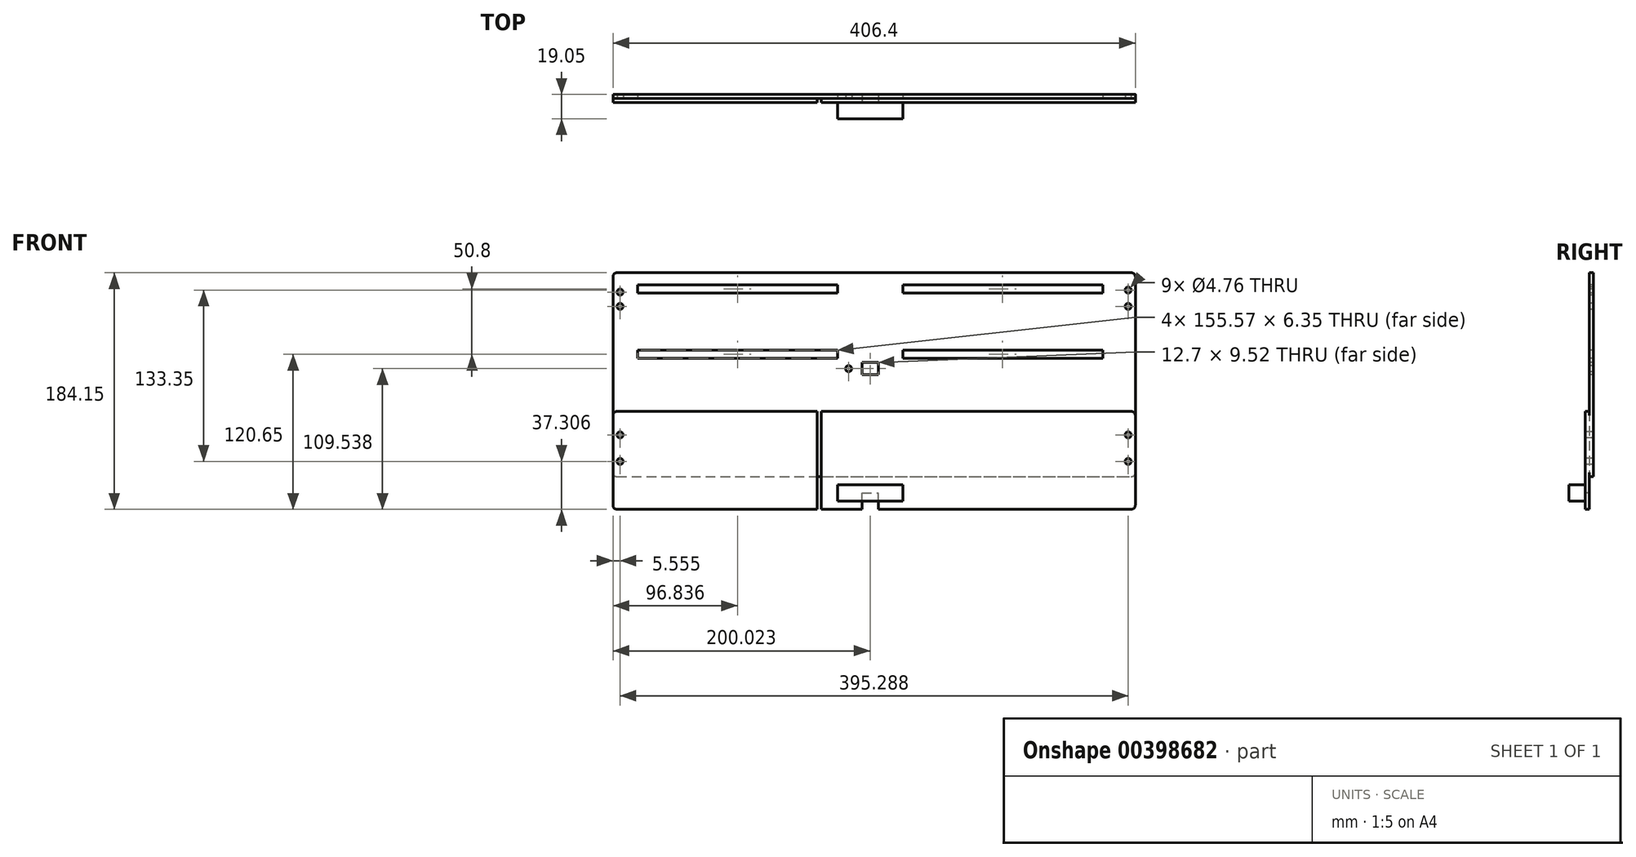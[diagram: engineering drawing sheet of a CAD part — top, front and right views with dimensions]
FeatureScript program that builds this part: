
annotation { "Feature Type Name" : "Feature", "Feature Type Description" : "" }
export const myFeature = defineFeature(function(context is Context, id is Id, definition is map)
    precondition{}
    {
        {
            var Q0;
            Q0=qCreatedBy(makeId("Front.planeOp"),FACE);
            var sketch = newSketch(context, id + "F0", { "sketchPlane" : qUnion([Q0])});
            skLineSegment(sketch, "E0.bottom", {"start": v(-194.67, 58.2) * mm, "end": v(211.73, 58.2) * mm});
            skLineSegment(sketch, "E0.top", {"start": v(-194.67, -100.56) * mm, "end": v(211.73, -100.56) * mm});
            skLineSegment(sketch, "E0.left", {"start": v(-194.67, 58.2) * mm, "end": v(-194.67, -100.56) * mm});
            skLineSegment(sketch, "E0.right", {"start": v(211.73, 58.2) * mm, "end": v(211.73, -100.56) * mm});
            skSolve(sketch);
        }
        {
            var Q0;
            Q0 = qSketchRegion(id + "F0", true);
            extrude(context, id + "F1", {"entities" : qUnion([Q0]), "depth" : 3.17 * mm});
        }
        {
            var Q0;
            Q0=makeQuery(id+"F1.opExtrude","SWEPT_EDGE",EDGE,{"disambiguationData":[OSD([sQuery(id+"F0.wireOp",EDGE,"E0.bottom"),sQuery(id+"F0.wireOp",EDGE,"E0.left")])]});
            fillet(context, id + "F2", {"entities" : qUnion([Q0]), "radius" : 3.17 * mm, "tangentPropagation" : true, "allowEdgeOverflow" : false});
        }
        {
            var Q0;
            Q0=makeQuery(id+"F1.opExtrude","SWEPT_EDGE",EDGE,{"disambiguationData":[OSD([sQuery(id+"F0.wireOp",EDGE,"E0.bottom"),sQuery(id+"F0.wireOp",EDGE,"E0.right")])]});
            fillet(context, id + "F3", {"entities" : qUnion([Q0]), "radius" : 3.17 * mm, "tangentPropagation" : true, "allowEdgeOverflow" : false});
        }
        {
            var Q0;
            Q0=makeQuery(id+"F1.opExtrude","SWEPT_EDGE",EDGE,{"disambiguationData":[OSD([sQuery(id+"F0.wireOp",EDGE,"E0.top"),sQuery(id+"F0.wireOp",EDGE,"E0.right")])]});
            fillet(context, id + "F4", {"entities" : qUnion([Q0]), "radius" : 3.17 * mm, "tangentPropagation" : true, "allowEdgeOverflow" : false});
        }
        {
            var Q0;
            Q0=makeQuery(id+"F1.opExtrude","SWEPT_EDGE",EDGE,{"disambiguationData":[OSD([sQuery(id+"F0.wireOp",EDGE,"E0.top"),sQuery(id+"F0.wireOp",EDGE,"E0.left")])]});
            fillet(context, id + "F5", {"entities" : qUnion([Q0]), "radius" : 3.17 * mm, "tangentPropagation" : true, "allowEdgeOverflow" : false});
        }
        {
            var Q0;
            Q0=makeQuery(id+"F1.opExtrude","CAP_FACE",FACE,{"disambiguationData":[OSD([sQuery(id+"F0.wireOp",EDGE,"E0.bottom"),sQuery(id+"F0.wireOp",EDGE,"E0.top"),sQuery(id+"F0.wireOp",EDGE,"E0.left"),sQuery(id+"F0.wireOp",EDGE,"E0.right")])],"isStart":false});
            var sketch = newSketch(context, id + "F6", { "sketchPlane" : qUnion([Q0])});
            skLineSegment(sketch, "E1.bottom", {"start": v(-175.62, 48.67) * mm, "end": v(-20.05, 48.67) * mm});
            skLineSegment(sketch, "E1.top", {"start": v(-175.62, 42.32) * mm, "end": v(-20.05, 42.32) * mm});
            skLineSegment(sketch, "E1.left", {"start": v(-175.62, 48.67) * mm, "end": v(-175.62, 42.32) * mm});
            skLineSegment(sketch, "E1.right", {"start": v(-20.05, 48.67) * mm, "end": v(-20.05, 42.32) * mm});
            skSolve(sketch);
        }
        {
            var Q0;
            Q0=makeQuery(id+"F6.imprint","IMPRINT",FACE,{"disambiguationData":[TD([[makeQuery(id+"F6.imprint","IMPRINT",EDGE,{"derivedFrom":sQuery(id+"F6.wireOp",EDGE,"E1.bottom")}),-1.0]])]});
            extrude(context, id + "F7", {"entities" : qUnion([Q0]), "operationType" : NewBodyOperationType.REMOVE, "oppositeDirection" : true, "depth" : 3.17 * mm});
        }
        {
            var Q0;
            Q0=makeQuery(id+"F1.opExtrude","CAP_FACE",FACE,{"disambiguationData":[OSD([sQuery(id+"F0.wireOp",EDGE,"E0.bottom"),sQuery(id+"F0.wireOp",EDGE,"E0.top"),sQuery(id+"F0.wireOp",EDGE,"E0.left"),sQuery(id+"F0.wireOp",EDGE,"E0.right")])],"isStart":false});
            var sketch = newSketch(context, id + "F8", { "sketchPlane" : qUnion([Q0])});
            skLineSegment(sketch, "E2.bottom", {"start": v(-175.62, -2.13) * mm, "end": v(-20.05, -2.13) * mm});
            skLineSegment(sketch, "E2.top", {"start": v(-175.62, -8.48) * mm, "end": v(-20.05, -8.48) * mm});
            skLineSegment(sketch, "E2.left", {"start": v(-175.62, -2.13) * mm, "end": v(-175.62, -8.48) * mm});
            skLineSegment(sketch, "E2.right", {"start": v(-20.05, -2.13) * mm, "end": v(-20.05, -8.48) * mm});
            skSolve(sketch);
        }
        {
            var Q0;
            Q0 = qSketchRegion(id + "F8", true);
            extrude(context, id + "F9", {"entities" : qUnion([Q0]), "operationType" : NewBodyOperationType.REMOVE, "oppositeDirection" : true, "depth" : 3.17 * mm});
        }
        {
            var Q0;
            Q0=makeQuery(id+"F1.opExtrude","CAP_FACE",FACE,{"disambiguationData":[OSD([sQuery(id+"F0.wireOp",EDGE,"E0.bottom"),sQuery(id+"F0.wireOp",EDGE,"E0.top"),sQuery(id+"F0.wireOp",EDGE,"E0.left"),sQuery(id+"F0.wireOp",EDGE,"E0.right")])],"isStart":false});
            var sketch = newSketch(context, id + "F10", { "sketchPlane" : qUnion([Q0])});
            skLineSegment(sketch, "E3.bottom", {"start": v(30.75, 48.67) * mm, "end": v(186.33, 48.67) * mm});
            skLineSegment(sketch, "E3.top", {"start": v(30.75, 42.32) * mm, "end": v(186.33, 42.32) * mm});
            skLineSegment(sketch, "E3.left", {"start": v(30.75, 48.67) * mm, "end": v(30.75, 42.32) * mm});
            skLineSegment(sketch, "E3.right", {"start": v(186.33, 48.67) * mm, "end": v(186.33, 42.32) * mm});
            skSolve(sketch);
        }
        {
            var Q0;
            Q0 = qSketchRegion(id + "F10", true);
            extrude(context, id + "F11", {"entities" : qUnion([Q0]), "operationType" : NewBodyOperationType.REMOVE, "oppositeDirection" : true, "depth" : 3.17 * mm});
        }
        {
            var Q0;
            Q0=makeQuery(id+"F1.opExtrude","CAP_FACE",FACE,{"disambiguationData":[OSD([sQuery(id+"F0.wireOp",EDGE,"E0.bottom"),sQuery(id+"F0.wireOp",EDGE,"E0.top"),sQuery(id+"F0.wireOp",EDGE,"E0.left"),sQuery(id+"F0.wireOp",EDGE,"E0.right")])],"isStart":false});
            var sketch = newSketch(context, id + "F12", { "sketchPlane" : qUnion([Q0])});
            skLineSegment(sketch, "E4.bottom", {"start": v(30.75, -2.13) * mm, "end": v(186.33, -2.13) * mm});
            skLineSegment(sketch, "E4.top", {"start": v(30.75, -8.48) * mm, "end": v(186.33, -8.48) * mm});
            skLineSegment(sketch, "E4.left", {"start": v(30.75, -2.13) * mm, "end": v(30.75, -8.48) * mm});
            skLineSegment(sketch, "E4.right", {"start": v(186.33, -2.13) * mm, "end": v(186.33, -8.48) * mm});
            skSolve(sketch);
        }
        {
            var Q0;
            Q0 = qSketchRegion(id + "F12", true);
            extrude(context, id + "F13", {"entities" : qUnion([Q0]), "operationType" : NewBodyOperationType.REMOVE, "oppositeDirection" : true, "depth" : 25.4 * mm});
        }
        {
            var Q0;
            Q0=makeQuery(id+"F1.opExtrude","CAP_FACE",FACE,{"disambiguationData":[OSD([sQuery(id+"F0.wireOp",EDGE,"E0.bottom"),sQuery(id+"F0.wireOp",EDGE,"E0.top"),sQuery(id+"F0.wireOp",EDGE,"E0.left"),sQuery(id+"F0.wireOp",EDGE,"E0.right")])],"isStart":false});
            var sketch = newSketch(context, id + "F14", { "sketchPlane" : qUnion([Q0])});
            skLineSegment(sketch, "E5.bottom", {"start": v(-1, -11.66) * mm, "end": v(11.7, -11.66) * mm});
            skLineSegment(sketch, "E5.top", {"start": v(-1, -21.18) * mm, "end": v(11.7, -21.18) * mm});
            skLineSegment(sketch, "E5.left", {"start": v(-1, -11.66) * mm, "end": v(-1, -21.18) * mm});
            skLineSegment(sketch, "E5.right", {"start": v(11.7, -11.66) * mm, "end": v(11.7, -21.18) * mm});
            skSolve(sketch);
        }
        {
            var Q0;
            Q0 = qSketchRegion(id + "F14", true);
            extrude(context, id + "F15", {"entities" : qUnion([Q0]), "operationType" : NewBodyOperationType.REMOVE, "oppositeDirection" : true, "depth" : 25.4 * mm});
        }
        {
            var Q0;
            Q0=makeQuery(id+"F1.opExtrude","CAP_FACE",FACE,{"disambiguationData":[OSD([sQuery(id+"F0.wireOp",EDGE,"E0.bottom"),sQuery(id+"F0.wireOp",EDGE,"E0.top"),sQuery(id+"F0.wireOp",EDGE,"E0.left"),sQuery(id+"F0.wireOp",EDGE,"E0.right")])],"isStart":false});
            var sketch = newSketch(context, id + "F16", { "sketchPlane" : qUnion([Q0])});
            skCircle(sketch, "E6", {"center": v(-11.32, -16.47) * mm, "radius": 2.38 * mm});
            skSolve(sketch);
        }
        {
            var Q0;
            Q0 = qSketchRegion(id + "F16", true);
            extrude(context, id + "F17", {"entities" : qUnion([Q0]), "operationType" : NewBodyOperationType.REMOVE, "oppositeDirection" : true, "depth" : 3.17 * mm});
        }
        {
            var Q0;
            Q0=makeQuery(id+"F1.opExtrude","CAP_FACE",FACE,{"disambiguationData":[OSD([sQuery(id+"F0.wireOp",EDGE,"E0.bottom"),sQuery(id+"F0.wireOp",EDGE,"E0.top"),sQuery(id+"F0.wireOp",EDGE,"E0.left"),sQuery(id+"F0.wireOp",EDGE,"E0.right")])],"isStart":false});
            var sketch = newSketch(context, id + "F18", { "sketchPlane" : qUnion([Q0])});
            skCircle(sketch, "E7", {"center": v(-189.12, 43.1) * mm, "radius": 2.38 * mm});
            skCircle(sketch, "E8", {"center": v(-189.12, 32) * mm, "radius": 2.38 * mm});
            skSolve(sketch);
        }
        {
            var Q0;
            Q0 = qSketchRegion(id + "F18", true);
            extrude(context, id + "F19", {"entities" : qUnion([Q0]), "operationType" : NewBodyOperationType.REMOVE, "oppositeDirection" : true, "depth" : 25.4 * mm});
        }
        {
            var Q0;
            Q0=makeQuery(id+"F1.opExtrude","CAP_FACE",FACE,{"disambiguationData":[OSD([sQuery(id+"F0.wireOp",EDGE,"E0.bottom"),sQuery(id+"F0.wireOp",EDGE,"E0.top"),sQuery(id+"F0.wireOp",EDGE,"E0.left"),sQuery(id+"F0.wireOp",EDGE,"E0.right")])],"isStart":false});
            var sketch = newSketch(context, id + "F20", { "sketchPlane" : qUnion([Q0])});
            skCircle(sketch, "E9", {"center": v(206.17, 44.7) * mm, "radius": 2.38 * mm});
            skCircle(sketch, "E10", {"center": v(206.17, 32) * mm, "radius": 2.38 * mm});
            skSolve(sketch);
        }
        {
            var Q0;
            Q0=makeQuery(id+"F20.imprint","IMPRINT",FACE,{"disambiguationData":[TD([[makeQuery(id+"F20.imprint","IMPRINT",EDGE,{"derivedFrom":sQuery(id+"F20.wireOp",EDGE,"E9")}),1.0]])]});
            var Q1;
            Q1=makeQuery(id+"F20.imprint","IMPRINT",FACE,{"disambiguationData":[TD([[makeQuery(id+"F20.imprint","IMPRINT",EDGE,{"derivedFrom":sQuery(id+"F20.wireOp",EDGE,"E10")}),1.0]])]});
            extrude(context, id + "F21", {"entities" : qUnion([Q0, Q1]), "operationType" : NewBodyOperationType.REMOVE, "oppositeDirection" : true, "depth" : 25.4 * mm});
        }
        {
            var Q0;
            Q0=makeQuery(id+"F1.opExtrude","CAP_FACE",FACE,{"disambiguationData":[OSD([sQuery(id+"F0.wireOp",EDGE,"E0.bottom"),sQuery(id+"F0.wireOp",EDGE,"E0.top"),sQuery(id+"F0.wireOp",EDGE,"E0.left"),sQuery(id+"F0.wireOp",EDGE,"E0.right")])],"isStart":false});
            var sketch = newSketch(context, id + "F22", { "sketchPlane" : qUnion([Q0])});
            skLineSegment(sketch, "E11.bottom", {"start": v(-194.67, -49.76) * mm, "end": v(211.73, -49.76) * mm});
            skLineSegment(sketch, "E11.top", {"start": v(-194.67, -125.96) * mm, "end": v(211.73, -125.96) * mm});
            skLineSegment(sketch, "E11.left", {"start": v(-194.67, -49.76) * mm, "end": v(-194.67, -125.96) * mm});
            skLineSegment(sketch, "E11.right", {"start": v(211.73, -49.76) * mm, "end": v(211.73, -125.96) * mm});
            skSolve(sketch);
        }
        {
            var Q0;
            Q0 = qSketchRegion(id + "F22", true);
            extrude(context, id + "F23", {"entities" : qUnion([Q0]), "operationType" : NewBodyOperationType.ADD, "depth" : 3.17 * mm});
        }
        {
            var Q0;
            Q0=makeQuery(id+"F23.opExtrude","SWEPT_EDGE",EDGE,{"disambiguationData":[OSD([sQuery(id+"F22.wireOp",EDGE,"E11.top"),sQuery(id+"F22.wireOp",EDGE,"E11.left")])]});
            var Q1;
            Q1=makeQuery(id+"F23.opExtrude","SWEPT_EDGE",EDGE,{"disambiguationData":[OSD([sQuery(id+"F22.wireOp",EDGE,"E11.top"),sQuery(id+"F22.wireOp",EDGE,"E11.right")])]});
            fillet(context, id + "F24", {"entities" : qUnion([Q0, Q1]), "radius" : 3.17 * mm, "tangentPropagation" : true, "allowEdgeOverflow" : false});
        }
        {
            var Q0;
            Q0=makeQuery(id+"F23.opExtrude","SWEPT_EDGE",EDGE,{"disambiguationData":[OSD([sQuery(id+"F0.wireOp",EDGE,"E0.right"),sQuery(id+"F22.wireOp",EDGE,"E11.bottom"),sQuery(id+"F22.wireOp",EDGE,"E11.right")])]});
            var Q1;
            Q1=makeQuery(id+"F23.opExtrude","SWEPT_EDGE",EDGE,{"disambiguationData":[OSD([sQuery(id+"F0.wireOp",EDGE,"E0.left"),sQuery(id+"F22.wireOp",EDGE,"E11.bottom"),sQuery(id+"F22.wireOp",EDGE,"E11.left")])]});
            fillet(context, id + "F25", {"entities" : qUnion([Q0, Q1]), "radius" : 3.17 * mm, "tangentPropagation" : true, "allowEdgeOverflow" : false});
        }
        {
            var Q0;
            Q0=makeQuery(id+"F23.opExtrude","CAP_FACE",FACE,{"disambiguationData":[OSD([sQuery(id+"F22.wireOp",EDGE,"E11.bottom"),sQuery(id+"F22.wireOp",EDGE,"E11.top"),sQuery(id+"F22.wireOp",EDGE,"E11.left"),sQuery(id+"F22.wireOp",EDGE,"E11.right")])],"isStart":false});
            var sketch = newSketch(context, id + "F26", { "sketchPlane" : qUnion([Q0])});
            skLineSegment(sketch, "E12.bottom", {"start": v(-1, -125.96) * mm, "end": v(11.7, -125.96) * mm});
            skLineSegment(sketch, "E12.top", {"start": v(-1, -113.26) * mm, "end": v(11.7, -113.26) * mm});
            skLineSegment(sketch, "E12.left", {"start": v(-1, -125.96) * mm, "end": v(-1, -113.26) * mm});
            skLineSegment(sketch, "E12.right", {"start": v(11.7, -125.96) * mm, "end": v(11.7, -113.26) * mm});
            skSolve(sketch);
        }
        {
            var Q0;
            Q0 = qSketchRegion(id + "F26", true);
            extrude(context, id + "F27", {"entities" : qUnion([Q0]), "operationType" : NewBodyOperationType.REMOVE, "oppositeDirection" : true, "depth" : 25.4 * mm});
        }
        {
            var Q0;
            Q0=makeQuery(id+"F23.opExtrude","CAP_FACE",FACE,{"disambiguationData":[OSD([sQuery(id+"F22.wireOp",EDGE,"E11.bottom"),sQuery(id+"F22.wireOp",EDGE,"E11.top"),sQuery(id+"F22.wireOp",EDGE,"E11.left"),sQuery(id+"F22.wireOp",EDGE,"E11.right")])],"isStart":false});
            var sketch = newSketch(context, id + "F28", { "sketchPlane" : qUnion([Q0])});
            skCircle(sketch, "E13", {"center": v(206.17, -68.02) * mm, "radius": 2.38 * mm});
            skCircle(sketch, "E14", {"center": v(206.17, -88.65) * mm, "radius": 2.38 * mm});
            skCircle(sketch, "E15", {"center": v(-189.12, -68.02) * mm, "radius": 2.38 * mm});
            skCircle(sketch, "E16", {"center": v(-189.12, -88.65) * mm, "radius": 2.38 * mm});
            skSolve(sketch);
        }
        {
            var Q0;
            Q0 = qSketchRegion(id + "F28", true);
            extrude(context, id + "F29", {"entities" : qUnion([Q0]), "operationType" : NewBodyOperationType.REMOVE, "oppositeDirection" : true, "depth" : 25.4 * mm});
        }
        {
            var Q0;
            Q0=makeQuery(id+"F23.opExtrude","CAP_FACE",FACE,{"disambiguationData":[OSD([sQuery(id+"F22.wireOp",EDGE,"E11.bottom"),sQuery(id+"F22.wireOp",EDGE,"E11.top"),sQuery(id+"F22.wireOp",EDGE,"E11.left"),sQuery(id+"F22.wireOp",EDGE,"E11.right")])],"isStart":false});
            var sketch = newSketch(context, id + "F30", { "sketchPlane" : qUnion([Q0])});
            skPoint(sketch, "E17.oppositeSnap0", {"position": v(11.7, -119.6) * mm});
            skLineSegment(sketch, "E17.bottom", {"start": v(-20.05, -106.9) * mm, "end": v(30.75, -106.9) * mm});
            skLineSegment(sketch, "E17.top", {"start": v(-20.05, -119.6) * mm, "end": v(30.75, -119.6) * mm});
            skLineSegment(sketch, "E17.left", {"start": v(-20.05, -106.9) * mm, "end": v(-20.05, -119.6) * mm});
            skLineSegment(sketch, "E17.right", {"start": v(30.75, -106.9) * mm, "end": v(30.75, -119.6) * mm});
            skSolve(sketch);
        }
        {
            var Q0;
            Q0 = qSketchRegion(id + "F30", true);
            extrude(context, id + "F31", {"entities" : qUnion([Q0]), "operationType" : NewBodyOperationType.ADD, "depth" : 12.7 * mm});
        }
        {
            var Q0;
            Q0=makeQuery(id+"F23.opExtrude","CAP_FACE",FACE,{"disambiguationData":[OSD([sQuery(id+"F22.wireOp",EDGE,"E11.bottom"),sQuery(id+"F22.wireOp",EDGE,"E11.top"),sQuery(id+"F22.wireOp",EDGE,"E11.left"),sQuery(id+"F22.wireOp",EDGE,"E11.right")])],"isStart":false});
            var sketch = newSketch(context, id + "F32", { "sketchPlane" : qUnion([Q0])});
            skLineSegment(sketch, "E18.bottom", {"start": v(-35.92, -49.76) * mm, "end": v(-32.75, -49.76) * mm});
            skLineSegment(sketch, "E18.top", {"start": v(-35.92, -125.96) * mm, "end": v(-32.75, -125.96) * mm});
            skLineSegment(sketch, "E18.left", {"start": v(-35.92, -49.76) * mm, "end": v(-35.92, -125.96) * mm});
            skLineSegment(sketch, "E18.right", {"start": v(-32.75, -49.76) * mm, "end": v(-32.75, -125.96) * mm});
            skSolve(sketch);
        }
        {
            var Q0;
            Q0 = qSketchRegion(id + "F32", true);
            extrude(context, id + "F33", {"entities" : qUnion([Q0]), "operationType" : NewBodyOperationType.REMOVE, "oppositeDirection" : true, "depth" : 3.17 * mm});
        }
    });
